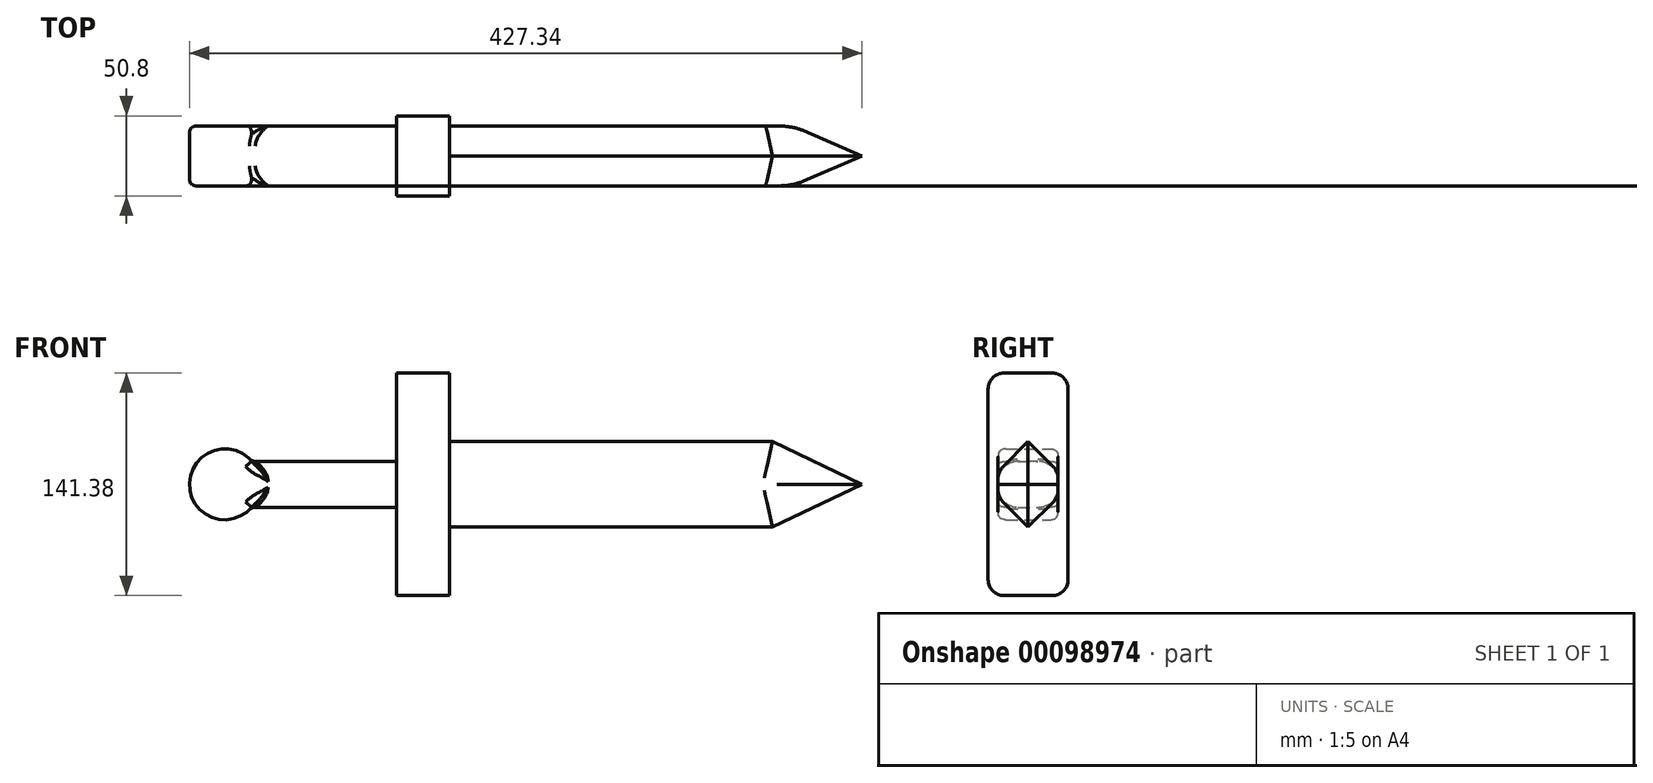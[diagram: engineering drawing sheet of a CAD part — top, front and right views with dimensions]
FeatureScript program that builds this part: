
annotation { "Feature Type Name" : "Feature", "Feature Type Description" : "" }
export const myFeature = defineFeature(function(context is Context, id is Id, definition is map)
    precondition{}
    {
        {
            var Q0;
            Q0=qCreatedBy(makeId("Front.planeOp"),FACE);
            var sketch = newSketch(context, id + "F0", { "sketchPlane" : qUnion([Q0])});
            skLineSegment(sketch, "E0.bottom", {"start": v(-62.96, 14.57) * mm, "end": v(62.96, 14.57) * mm});
            skLineSegment(sketch, "E0.top", {"start": v(-62.96, -14.57) * mm, "end": v(62.96, -14.57) * mm});
            skLineSegment(sketch, "E0.left", {"start": v(-62.96, 14.57) * mm, "end": v(-62.96, -14.57) * mm});
            skLineSegment(sketch, "E0.right", {"start": v(62.96, 14.57) * mm, "end": v(62.96, -14.57) * mm});
            skPoint(sketch, "E0.middle", {"position": v(0, 0) * mm});
            skCircle(sketch, "E1", {"center": v(-62.96, 0) * mm, "radius": 22.51 * mm});
            skLineSegment(sketch, "E2.bottom", {"start": v(79.87, 70.7) * mm, "end": v(46.05, 70.7) * mm});
            skLineSegment(sketch, "E2.top", {"start": v(79.87, -70.7) * mm, "end": v(46.05, -70.7) * mm});
            skLineSegment(sketch, "E2.left", {"start": v(79.87, 70.7) * mm, "end": v(79.87, -70.7) * mm});
            skLineSegment(sketch, "E2.right", {"start": v(46.05, 70.7) * mm, "end": v(46.05, -70.7) * mm});
            skPoint(sketch, "E2.middle", {"position": v(62.96, 0) * mm});
            skLineSegment(sketch, "E3.bottom", {"start": v(79.87, -27.16) * mm, "end": v(284.93, -27.16) * mm});
            skLineSegment(sketch, "E3.top", {"start": v(79.87, 27.16) * mm, "end": v(284.93, 27.16) * mm});
            skLineSegment(sketch, "E3.left", {"start": v(79.87, -27.16) * mm, "end": v(79.87, 27.16) * mm});
            skLineSegment(sketch, "E3.right", {"start": v(284.93, -27.16) * mm, "end": v(284.93, 27.16) * mm});
            skPoint(sketch, "E3.middle", {"position": v(182.4, 0) * mm});
            skLineSegment(sketch, "E4", {"start": v(284.93, -27.16) * mm, "end": v(341.87, 0) * mm});
            skLineSegment(sketch, "E5", {"start": v(341.87, 0) * mm, "end": v(284.93, 27.16) * mm});
            skSolve(sketch);
        }
        {
            var Q0;
            {var subQ1=sQuery(id+"F0.wireOp",EDGE,"E0.right");Q0=makeQuery(id+"F0.imprint","IMPRINT",FACE,{"disambiguationData":[TD([[makeQuery(id+"F0.imprint","IMPRINT",EDGE,{"derivedFrom":subQ1}),1.0]])]});}
            var Q1;
            {var subQ0=sQuery(id+"F0.wireOp",EDGE,"E0.right");Q1=makeQuery(id+"F0.imprint","IMPRINT",FACE,{"disambiguationData":[TD([[makeQuery(id+"F0.imprint","IMPRINT",EDGE,{"derivedFrom":subQ0}),-1.0]])]});}
            extrude(context, id + "F1", {"entities" : qUnion([Q0, Q1]), "endBound" : BoundingType.SYMMETRIC, "depth" : 50.8 * mm});
        }
        {
            var Q0;
            Q0 = qSketchRegion(id + "F0", true);
            extrude(context, id + "F2", {"entities" : qUnion([Q0]), "operationType" : NewBodyOperationType.ADD, "endBound" : BoundingType.SYMMETRIC, "depth" : 38.1 * mm});
        }
        {
            var Q0;
            Q0=makeQuery(id+"F1.opExtrude","CAP_EDGE",EDGE,{"disambiguationData":[OSD([sQuery(id+"F0.wireOp",EDGE,"E2.bottom")])],"isStart":false});
            var Q1;
            Q1=makeQuery(id+"F1.opExtrude","CAP_EDGE",EDGE,{"disambiguationData":[OSD([sQuery(id+"F0.wireOp",EDGE,"E2.bottom")])],"isStart":true});
            var Q2;
            Q2=makeQuery(id+"F1.opExtrude","CAP_EDGE",EDGE,{"disambiguationData":[OSD([sQuery(id+"F0.wireOp",EDGE,"E2.top")])],"isStart":true});
            var Q3;
            Q3=makeQuery(id+"F1.opExtrude","CAP_EDGE",EDGE,{"disambiguationData":[OSD([sQuery(id+"F0.wireOp",EDGE,"E2.top")])],"isStart":false});
            fillet(context, id + "F3", {"entities" : qUnion([Q0, Q1, Q2, Q3]), "radius" : 10.16 * mm, "tangentPropagation" : true, "allowEdgeOverflow" : false});
        }
        {
            var Q0;
            Q0=makeQuery(id+"F2.opExtrude","CAP_EDGE",EDGE,{"disambiguationData":[OSD([sQuery(id+"F0.wireOp",EDGE,"E0.bottom")])],"isStart":false});
            var Q1;
            Q1=makeQuery(id+"F2.opExtrude","CAP_EDGE",EDGE,{"disambiguationData":[OSD([sQuery(id+"F0.wireOp",EDGE,"E0.top")])],"isStart":false});
            var Q2;
            Q2=makeQuery(id+"F2.opExtrude","CAP_EDGE",EDGE,{"disambiguationData":[OSD([sQuery(id+"F0.wireOp",EDGE,"E0.top")])],"isStart":true});
            var Q3;
            Q3=makeQuery(id+"F2.opExtrude","CAP_EDGE",EDGE,{"disambiguationData":[OSD([sQuery(id+"F0.wireOp",EDGE,"E0.bottom")])],"isStart":true});
            fillet(context, id + "F4", {"entities" : qUnion([Q0, Q1, Q2, Q3]), "radius" : 12.7 * mm, "tangentPropagation" : true, "allowEdgeOverflow" : false});
        }
        {
            var Q0;
            Q0=makeQuery(id+"F2.opExtrude","CAP_EDGE",EDGE,{"disambiguationData":[OSD([sQuery(id+"F0.wireOp",EDGE,"E3.top")])],"isStart":true});
            var Q1;
            Q1=makeQuery(id+"F2.opExtrude","CAP_EDGE",EDGE,{"disambiguationData":[OSD([sQuery(id+"F0.wireOp",EDGE,"E3.top")])],"isStart":false});
            var Q2;
            Q2=makeQuery(id+"F2.opExtrude","CAP_EDGE",EDGE,{"disambiguationData":[OSD([sQuery(id+"F0.wireOp",EDGE,"E3.bottom")])],"isStart":true});
            var Q3;
            Q3=makeQuery(id+"F2.opExtrude","CAP_EDGE",EDGE,{"disambiguationData":[OSD([sQuery(id+"F0.wireOp",EDGE,"E3.bottom")])],"isStart":false});
            chamfer(context, id + "F5", {"entities" : qUnion([Q0, Q1, Q2, Q3]), "width" : 19.05 * mm, "tangentPropagation" : true});
        }
        {
            var Q0;
            Q0=makeQuery(id+"F2.opExtrude","CAP_EDGE",EDGE,{"disambiguationData":[OSD([sQuery(id+"F0.wireOp",EDGE,"E4")])],"isStart":true});
            var Q1;
            Q1=makeQuery(id+"F2.opExtrude","CAP_EDGE",EDGE,{"disambiguationData":[OSD([sQuery(id+"F0.wireOp",EDGE,"E4")])],"isStart":false});
            var Q2;
            Q2=makeQuery(id+"F2.opExtrude","CAP_EDGE",EDGE,{"disambiguationData":[OSD([sQuery(id+"F0.wireOp",EDGE,"E5")])],"isStart":false});
            var Q3;
            Q3=makeQuery(id+"F2.opExtrude","CAP_EDGE",EDGE,{"disambiguationData":[OSD([sQuery(id+"F0.wireOp",EDGE,"E5")])],"isStart":true});
            chamfer(context, id + "F6", {"entities" : qUnion([Q0, Q1, Q2, Q3]), "width" : 19.05 * mm, "tangentPropagation" : true});
        }
        {
            var Q0;
            {var subQ0=sQuery(id+"F0.wireOp",EDGE,"E4");var subQ1=sQuery(id+"F0.wireOp",EDGE,"E3.top");var subQ2=sQuery(id+"F0.wireOp",EDGE,"E3.bottom");var subQ3=sQuery(id+"F0.wireOp",EDGE,"E2.left");var subQ4=sQuery(id+"F0.wireOp",EDGE,"E5");Q0=makeQuery(id+"F5.opChamfer","BLEND_EDGE",EDGE,{"blendedFrom":[makeQuery(id+"F2.opExtrude","CAP_EDGE",EDGE,{"disambiguationData":[OSD([subQ2])],"isStart":true}),makeQuery(id+"F2.boolean.opBoolean","SPLIT",FACE,{"disambiguationData":[TD([makeQuery(id+"F2.opExtrude","SWEPT_FACE",FACE,{"disambiguationData":[OSD([subQ2])]})])],"derivedFrom":makeQuery(id+"F2.opExtrude","CAP_FACE",FACE,{"disambiguationData":[OSD([sQuery(id+"F0.wireOp",EDGE,"E0.bottom"),sQuery(id+"F0.wireOp",EDGE,"E0.top"),sQuery(id+"F0.wireOp",EDGE,"E1"),sQuery(id+"F0.wireOp",EDGE,"E2.bottom"),sQuery(id+"F0.wireOp",EDGE,"E2.top"),subQ3,sQuery(id+"F0.wireOp",EDGE,"E2.right"),subQ2,subQ1,subQ0,subQ4])],"isStart":true})})],"blendedInto":[makeQuery(id+"F2.boolean.opBoolean","SPLIT",FACE,{"disambiguationData":[TD([makeQuery(id+"F2.opExtrude","SWEPT_FACE",FACE,{"disambiguationData":[OSD([subQ2])]})])],"derivedFrom":makeQuery(id+"F2.opExtrude","CAP_FACE",FACE,{"disambiguationData":[OSD([sQuery(id+"F0.wireOp",EDGE,"E0.bottom"),sQuery(id+"F0.wireOp",EDGE,"E0.top"),sQuery(id+"F0.wireOp",EDGE,"E1"),sQuery(id+"F0.wireOp",EDGE,"E2.bottom"),sQuery(id+"F0.wireOp",EDGE,"E2.top"),subQ3,sQuery(id+"F0.wireOp",EDGE,"E2.right"),subQ2,subQ1,subQ0,subQ4])],"isStart":true})})]});}
            var Q1;
            {var subQ0=sQuery(id+"F0.wireOp",EDGE,"E4");var subQ1=sQuery(id+"F0.wireOp",EDGE,"E3.top");var subQ2=sQuery(id+"F0.wireOp",EDGE,"E3.bottom");var subQ3=sQuery(id+"F0.wireOp",EDGE,"E2.left");var subQ4=sQuery(id+"F0.wireOp",EDGE,"E5");Q1=makeQuery(id+"F5.opChamfer","BLEND_EDGE",EDGE,{"blendedFrom":[makeQuery(id+"F2.opExtrude","CAP_EDGE",EDGE,{"disambiguationData":[OSD([subQ1])],"isStart":true}),makeQuery(id+"F2.boolean.opBoolean","SPLIT",FACE,{"disambiguationData":[TD([makeQuery(id+"F2.opExtrude","SWEPT_FACE",FACE,{"disambiguationData":[OSD([subQ2])]})])],"derivedFrom":makeQuery(id+"F2.opExtrude","CAP_FACE",FACE,{"disambiguationData":[OSD([sQuery(id+"F0.wireOp",EDGE,"E0.bottom"),sQuery(id+"F0.wireOp",EDGE,"E0.top"),sQuery(id+"F0.wireOp",EDGE,"E1"),sQuery(id+"F0.wireOp",EDGE,"E2.bottom"),sQuery(id+"F0.wireOp",EDGE,"E2.top"),subQ3,sQuery(id+"F0.wireOp",EDGE,"E2.right"),subQ2,subQ1,subQ0,subQ4])],"isStart":true})})],"blendedInto":[makeQuery(id+"F2.boolean.opBoolean","SPLIT",FACE,{"disambiguationData":[TD([makeQuery(id+"F2.opExtrude","SWEPT_FACE",FACE,{"disambiguationData":[OSD([subQ2])]})])],"derivedFrom":makeQuery(id+"F2.opExtrude","CAP_FACE",FACE,{"disambiguationData":[OSD([sQuery(id+"F0.wireOp",EDGE,"E0.bottom"),sQuery(id+"F0.wireOp",EDGE,"E0.top"),sQuery(id+"F0.wireOp",EDGE,"E1"),sQuery(id+"F0.wireOp",EDGE,"E2.bottom"),sQuery(id+"F0.wireOp",EDGE,"E2.top"),subQ3,sQuery(id+"F0.wireOp",EDGE,"E2.right"),subQ2,subQ1,subQ0,subQ4])],"isStart":true})})]});}
            var Q2;
            {var subQ0=sQuery(id+"F0.wireOp",EDGE,"E4");var subQ1=sQuery(id+"F0.wireOp",EDGE,"E3.top");var subQ2=sQuery(id+"F0.wireOp",EDGE,"E3.bottom");var subQ3=sQuery(id+"F0.wireOp",EDGE,"E2.left");var subQ4=sQuery(id+"F0.wireOp",EDGE,"E5");Q2=makeQuery(id+"F6.opChamfer","BLEND_EDGE",EDGE,{"blendedFrom":[makeQuery(id+"F2.opExtrude","CAP_EDGE",EDGE,{"disambiguationData":[OSD([subQ0])],"isStart":true}),makeQuery(id+"F2.boolean.opBoolean","SPLIT",FACE,{"disambiguationData":[TD([makeQuery(id+"F2.opExtrude","SWEPT_FACE",FACE,{"disambiguationData":[OSD([subQ2])]})])],"derivedFrom":makeQuery(id+"F2.opExtrude","CAP_FACE",FACE,{"disambiguationData":[OSD([sQuery(id+"F0.wireOp",EDGE,"E0.bottom"),sQuery(id+"F0.wireOp",EDGE,"E0.top"),sQuery(id+"F0.wireOp",EDGE,"E1"),sQuery(id+"F0.wireOp",EDGE,"E2.bottom"),sQuery(id+"F0.wireOp",EDGE,"E2.top"),subQ3,sQuery(id+"F0.wireOp",EDGE,"E2.right"),subQ2,subQ1,subQ0,subQ4])],"isStart":true})})],"blendedInto":[makeQuery(id+"F2.boolean.opBoolean","SPLIT",FACE,{"disambiguationData":[TD([makeQuery(id+"F2.opExtrude","SWEPT_FACE",FACE,{"disambiguationData":[OSD([subQ2])]})])],"derivedFrom":makeQuery(id+"F2.opExtrude","CAP_FACE",FACE,{"disambiguationData":[OSD([sQuery(id+"F0.wireOp",EDGE,"E0.bottom"),sQuery(id+"F0.wireOp",EDGE,"E0.top"),sQuery(id+"F0.wireOp",EDGE,"E1"),sQuery(id+"F0.wireOp",EDGE,"E2.bottom"),sQuery(id+"F0.wireOp",EDGE,"E2.top"),subQ3,sQuery(id+"F0.wireOp",EDGE,"E2.right"),subQ2,subQ1,subQ0,subQ4])],"isStart":true})})]});}
            var Q3;
            {var subQ0=sQuery(id+"F0.wireOp",EDGE,"E4");var subQ1=sQuery(id+"F0.wireOp",EDGE,"E3.top");var subQ2=sQuery(id+"F0.wireOp",EDGE,"E3.bottom");var subQ3=sQuery(id+"F0.wireOp",EDGE,"E2.left");var subQ4=sQuery(id+"F0.wireOp",EDGE,"E5");Q3=makeQuery(id+"F6.opChamfer","BLEND_EDGE",EDGE,{"blendedFrom":[makeQuery(id+"F2.opExtrude","CAP_EDGE",EDGE,{"disambiguationData":[OSD([subQ4])],"isStart":true}),makeQuery(id+"F2.boolean.opBoolean","SPLIT",FACE,{"disambiguationData":[TD([makeQuery(id+"F2.opExtrude","SWEPT_FACE",FACE,{"disambiguationData":[OSD([subQ2])]})])],"derivedFrom":makeQuery(id+"F2.opExtrude","CAP_FACE",FACE,{"disambiguationData":[OSD([sQuery(id+"F0.wireOp",EDGE,"E0.bottom"),sQuery(id+"F0.wireOp",EDGE,"E0.top"),sQuery(id+"F0.wireOp",EDGE,"E1"),sQuery(id+"F0.wireOp",EDGE,"E2.bottom"),sQuery(id+"F0.wireOp",EDGE,"E2.top"),subQ3,sQuery(id+"F0.wireOp",EDGE,"E2.right"),subQ2,subQ1,subQ0,subQ4])],"isStart":true})})],"blendedInto":[makeQuery(id+"F2.boolean.opBoolean","SPLIT",FACE,{"disambiguationData":[TD([makeQuery(id+"F2.opExtrude","SWEPT_FACE",FACE,{"disambiguationData":[OSD([subQ2])]})])],"derivedFrom":makeQuery(id+"F2.opExtrude","CAP_FACE",FACE,{"disambiguationData":[OSD([sQuery(id+"F0.wireOp",EDGE,"E0.bottom"),sQuery(id+"F0.wireOp",EDGE,"E0.top"),sQuery(id+"F0.wireOp",EDGE,"E1"),sQuery(id+"F0.wireOp",EDGE,"E2.bottom"),sQuery(id+"F0.wireOp",EDGE,"E2.top"),subQ3,sQuery(id+"F0.wireOp",EDGE,"E2.right"),subQ2,subQ1,subQ0,subQ4])],"isStart":true})})]});}
            fillet(context, id + "F7", {"entities" : qUnion([Q0, Q1, Q2, Q3]), "radius" : 10.16 * mm, "tangentPropagation" : true, "allowEdgeOverflow" : false});
        }
        {
            var Q0;
            {var subQ0=sQuery(id+"F0.wireOp",EDGE,"E4");var subQ1=sQuery(id+"F0.wireOp",EDGE,"E3.top");var subQ2=sQuery(id+"F0.wireOp",EDGE,"E3.bottom");var subQ3=sQuery(id+"F0.wireOp",EDGE,"E2.left");var subQ4=sQuery(id+"F0.wireOp",EDGE,"E5");Q0=makeQuery(id+"F5.opChamfer","BLEND_EDGE",EDGE,{"blendedFrom":[makeQuery(id+"F2.opExtrude","CAP_EDGE",EDGE,{"disambiguationData":[OSD([subQ2])],"isStart":false}),makeQuery(id+"F2.boolean.opBoolean","SPLIT",FACE,{"disambiguationData":[TD([makeQuery(id+"F2.opExtrude","SWEPT_FACE",FACE,{"disambiguationData":[OSD([subQ2])]})])],"derivedFrom":makeQuery(id+"F2.opExtrude","CAP_FACE",FACE,{"disambiguationData":[OSD([sQuery(id+"F0.wireOp",EDGE,"E0.bottom"),sQuery(id+"F0.wireOp",EDGE,"E0.top"),sQuery(id+"F0.wireOp",EDGE,"E1"),sQuery(id+"F0.wireOp",EDGE,"E2.bottom"),sQuery(id+"F0.wireOp",EDGE,"E2.top"),subQ3,sQuery(id+"F0.wireOp",EDGE,"E2.right"),subQ2,subQ1,subQ0,subQ4])],"isStart":false})})],"blendedInto":[makeQuery(id+"F2.boolean.opBoolean","SPLIT",FACE,{"disambiguationData":[TD([makeQuery(id+"F2.opExtrude","SWEPT_FACE",FACE,{"disambiguationData":[OSD([subQ2])]})])],"derivedFrom":makeQuery(id+"F2.opExtrude","CAP_FACE",FACE,{"disambiguationData":[OSD([sQuery(id+"F0.wireOp",EDGE,"E0.bottom"),sQuery(id+"F0.wireOp",EDGE,"E0.top"),sQuery(id+"F0.wireOp",EDGE,"E1"),sQuery(id+"F0.wireOp",EDGE,"E2.bottom"),sQuery(id+"F0.wireOp",EDGE,"E2.top"),subQ3,sQuery(id+"F0.wireOp",EDGE,"E2.right"),subQ2,subQ1,subQ0,subQ4])],"isStart":false})})]});}
            var Q1;
            {var subQ0=sQuery(id+"F0.wireOp",EDGE,"E4");var subQ1=sQuery(id+"F0.wireOp",EDGE,"E3.top");var subQ2=sQuery(id+"F0.wireOp",EDGE,"E3.bottom");var subQ3=sQuery(id+"F0.wireOp",EDGE,"E2.left");var subQ4=sQuery(id+"F0.wireOp",EDGE,"E5");Q1=makeQuery(id+"F5.opChamfer","BLEND_EDGE",EDGE,{"blendedFrom":[makeQuery(id+"F2.opExtrude","CAP_EDGE",EDGE,{"disambiguationData":[OSD([subQ1])],"isStart":false}),makeQuery(id+"F2.boolean.opBoolean","SPLIT",FACE,{"disambiguationData":[TD([makeQuery(id+"F2.opExtrude","SWEPT_FACE",FACE,{"disambiguationData":[OSD([subQ2])]})])],"derivedFrom":makeQuery(id+"F2.opExtrude","CAP_FACE",FACE,{"disambiguationData":[OSD([sQuery(id+"F0.wireOp",EDGE,"E0.bottom"),sQuery(id+"F0.wireOp",EDGE,"E0.top"),sQuery(id+"F0.wireOp",EDGE,"E1"),sQuery(id+"F0.wireOp",EDGE,"E2.bottom"),sQuery(id+"F0.wireOp",EDGE,"E2.top"),subQ3,sQuery(id+"F0.wireOp",EDGE,"E2.right"),subQ2,subQ1,subQ0,subQ4])],"isStart":false})})],"blendedInto":[makeQuery(id+"F2.boolean.opBoolean","SPLIT",FACE,{"disambiguationData":[TD([makeQuery(id+"F2.opExtrude","SWEPT_FACE",FACE,{"disambiguationData":[OSD([subQ2])]})])],"derivedFrom":makeQuery(id+"F2.opExtrude","CAP_FACE",FACE,{"disambiguationData":[OSD([sQuery(id+"F0.wireOp",EDGE,"E0.bottom"),sQuery(id+"F0.wireOp",EDGE,"E0.top"),sQuery(id+"F0.wireOp",EDGE,"E1"),sQuery(id+"F0.wireOp",EDGE,"E2.bottom"),sQuery(id+"F0.wireOp",EDGE,"E2.top"),subQ3,sQuery(id+"F0.wireOp",EDGE,"E2.right"),subQ2,subQ1,subQ0,subQ4])],"isStart":false})})]});}
            var Q2;
            {var subQ0=sQuery(id+"F0.wireOp",EDGE,"E4");var subQ1=sQuery(id+"F0.wireOp",EDGE,"E3.top");var subQ2=sQuery(id+"F0.wireOp",EDGE,"E3.bottom");var subQ3=sQuery(id+"F0.wireOp",EDGE,"E2.left");var subQ4=sQuery(id+"F0.wireOp",EDGE,"E5");Q2=makeQuery(id+"F6.opChamfer","BLEND_EDGE",EDGE,{"blendedFrom":[makeQuery(id+"F2.opExtrude","CAP_EDGE",EDGE,{"disambiguationData":[OSD([subQ4])],"isStart":false}),makeQuery(id+"F2.boolean.opBoolean","SPLIT",FACE,{"disambiguationData":[TD([makeQuery(id+"F2.opExtrude","SWEPT_FACE",FACE,{"disambiguationData":[OSD([subQ2])]})])],"derivedFrom":makeQuery(id+"F2.opExtrude","CAP_FACE",FACE,{"disambiguationData":[OSD([sQuery(id+"F0.wireOp",EDGE,"E0.bottom"),sQuery(id+"F0.wireOp",EDGE,"E0.top"),sQuery(id+"F0.wireOp",EDGE,"E1"),sQuery(id+"F0.wireOp",EDGE,"E2.bottom"),sQuery(id+"F0.wireOp",EDGE,"E2.top"),subQ3,sQuery(id+"F0.wireOp",EDGE,"E2.right"),subQ2,subQ1,subQ0,subQ4])],"isStart":false})})],"blendedInto":[makeQuery(id+"F2.boolean.opBoolean","SPLIT",FACE,{"disambiguationData":[TD([makeQuery(id+"F2.opExtrude","SWEPT_FACE",FACE,{"disambiguationData":[OSD([subQ2])]})])],"derivedFrom":makeQuery(id+"F2.opExtrude","CAP_FACE",FACE,{"disambiguationData":[OSD([sQuery(id+"F0.wireOp",EDGE,"E0.bottom"),sQuery(id+"F0.wireOp",EDGE,"E0.top"),sQuery(id+"F0.wireOp",EDGE,"E1"),sQuery(id+"F0.wireOp",EDGE,"E2.bottom"),sQuery(id+"F0.wireOp",EDGE,"E2.top"),subQ3,sQuery(id+"F0.wireOp",EDGE,"E2.right"),subQ2,subQ1,subQ0,subQ4])],"isStart":false})})]});}
            var Q3;
            {var subQ0=sQuery(id+"F0.wireOp",EDGE,"E4");var subQ1=sQuery(id+"F0.wireOp",EDGE,"E3.top");var subQ2=sQuery(id+"F0.wireOp",EDGE,"E3.bottom");var subQ3=sQuery(id+"F0.wireOp",EDGE,"E2.left");var subQ4=sQuery(id+"F0.wireOp",EDGE,"E5");Q3=makeQuery(id+"F6.opChamfer","BLEND_EDGE",EDGE,{"blendedFrom":[makeQuery(id+"F2.opExtrude","CAP_EDGE",EDGE,{"disambiguationData":[OSD([subQ0])],"isStart":false}),makeQuery(id+"F2.boolean.opBoolean","SPLIT",FACE,{"disambiguationData":[TD([makeQuery(id+"F2.opExtrude","SWEPT_FACE",FACE,{"disambiguationData":[OSD([subQ2])]})])],"derivedFrom":makeQuery(id+"F2.opExtrude","CAP_FACE",FACE,{"disambiguationData":[OSD([sQuery(id+"F0.wireOp",EDGE,"E0.bottom"),sQuery(id+"F0.wireOp",EDGE,"E0.top"),sQuery(id+"F0.wireOp",EDGE,"E1"),sQuery(id+"F0.wireOp",EDGE,"E2.bottom"),sQuery(id+"F0.wireOp",EDGE,"E2.top"),subQ3,sQuery(id+"F0.wireOp",EDGE,"E2.right"),subQ2,subQ1,subQ0,subQ4])],"isStart":false})})],"blendedInto":[makeQuery(id+"F2.boolean.opBoolean","SPLIT",FACE,{"disambiguationData":[TD([makeQuery(id+"F2.opExtrude","SWEPT_FACE",FACE,{"disambiguationData":[OSD([subQ2])]})])],"derivedFrom":makeQuery(id+"F2.opExtrude","CAP_FACE",FACE,{"disambiguationData":[OSD([sQuery(id+"F0.wireOp",EDGE,"E0.bottom"),sQuery(id+"F0.wireOp",EDGE,"E0.top"),sQuery(id+"F0.wireOp",EDGE,"E1"),sQuery(id+"F0.wireOp",EDGE,"E2.bottom"),sQuery(id+"F0.wireOp",EDGE,"E2.top"),subQ3,sQuery(id+"F0.wireOp",EDGE,"E2.right"),subQ2,subQ1,subQ0,subQ4])],"isStart":false})})]});}
            fillet(context, id + "F8", {"entities" : qUnion([Q0, Q1, Q2, Q3]), "radius" : 10.16 * mm, "tangentPropagation" : true, "allowEdgeOverflow" : false});
        }
        {
            var Q0;
            Q0=makeQuery(id+"F2.opExtrude","CAP_EDGE",EDGE,{"disambiguationData":[OSD([sQuery(id+"F0.wireOp",EDGE,"E1")])],"isStart":true});
            var Q1;
            Q1=makeQuery(id+"F2.opExtrude","SWEPT_FACE",FACE,{"disambiguationData":[OSD([sQuery(id+"F0.wireOp",EDGE,"E1")])]});
            var Q2;
            Q2=makeQuery(id+"F2.opExtrude","CAP_EDGE",EDGE,{"disambiguationData":[OSD([sQuery(id+"F0.wireOp",EDGE,"E1")])],"isStart":false});
            fillet(context, id + "F9", {"entities" : qUnion([Q0, Q1, Q2]), "radius" : 5.08 * mm, "tangentPropagation" : true, "rho" : 0.5, "crossSection" : FilletCrossSection.CONIC, "allowEdgeOverflow" : false});
        }
    });
